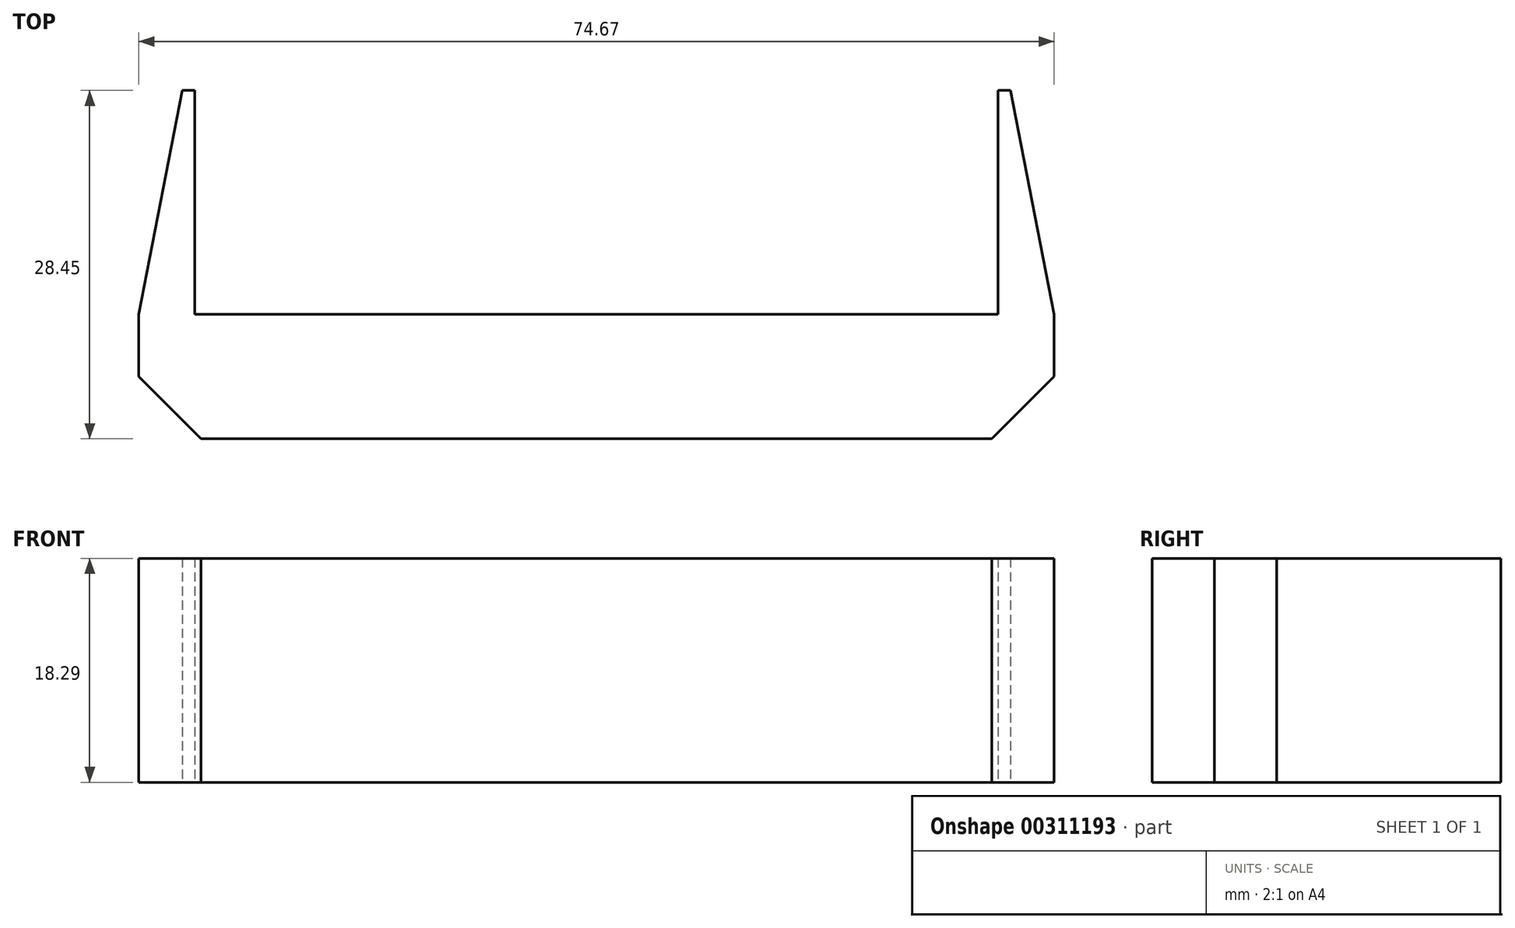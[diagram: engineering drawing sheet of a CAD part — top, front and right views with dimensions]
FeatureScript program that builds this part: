
annotation { "Feature Type Name" : "Feature", "Feature Type Description" : "" }
export const myFeature = defineFeature(function(context is Context, id is Id, definition is map)
    precondition{}
    {
        {
            var Q0;
            Q0=qCreatedBy(makeId("Top.planeOp"),FACE);
            var sketch = newSketch(context, id + "F0", { "sketchPlane" : qUnion([Q0])});
            skLineSegment(sketch, "E0.top", {"start": v(0, -18.29) * mm, "end": v(65.53, -18.29) * mm});
            skLineSegment(sketch, "E0.left", {"start": v(0, 0) * mm, "end": v(0, -18.29) * mm});
            skLineSegment(sketch, "E0.right", {"start": v(65.53, 0) * mm, "end": v(65.53, -18.29) * mm});
            skLineSegment(sketch, "E1", {"start": v(0, 0) * mm, "end": v(-1.02, 0) * mm});
            skLineSegment(sketch, "E2", {"start": v(66.55, 0) * mm, "end": v(65.53, 0) * mm});
            skLineSegment(sketch, "E3.top", {"start": v(-4.57, -28.45) * mm, "end": v(70.1, -28.45) * mm});
            skLineSegment(sketch, "E3.left", {"start": v(-4.57, -18.29) * mm, "end": v(-4.57, -28.45) * mm});
            skLineSegment(sketch, "E3.right", {"start": v(70.1, -18.29) * mm, "end": v(70.1, -28.45) * mm});
            skLineSegment(sketch, "E4", {"start": v(70.1, -18.29) * mm, "end": v(66.55, 0) * mm});
            skLineSegment(sketch, "E5", {"start": v(-4.57, -18.29) * mm, "end": v(-1.02, 0) * mm});
            skPoint(sketch, "E6.orphan", {"position": v(-2.03, 0) * mm});
            skPoint(sketch, "E7.0.end.orphan", {"position": v(-2.03, -18.29) * mm});
            skPoint(sketch, "E8.orphan", {"position": v(67.56, 0) * mm});
            skLineSegment(sketch, "E9.bottom", {"start": v(13.72, -28.45) * mm, "end": v(51.82, -28.45) * mm});
            skLineSegment(sketch, "E9.top", {"start": v(13.72, -79.25) * mm, "end": v(51.82, -79.25) * mm});
            skLineSegment(sketch, "E9.left", {"start": v(13.72, -28.45) * mm, "end": v(13.72, -79.25) * mm});
            skLineSegment(sketch, "E9.right", {"start": v(51.82, -28.45) * mm, "end": v(51.82, -79.25) * mm});
            skSolve(sketch);
        }
        {
            var Q0;
            Q0=makeQuery(id+"F0.imprint","IMPRINT",FACE,{"disambiguationData":[TD([[makeQuery(id+"F0.imprint","IMPRINT",EDGE,{"derivedFrom":sQuery(id+"F0.wireOp",EDGE,"E9.bottom")}),-1.0]])]});
            var Q1;
            Q1=makeQuery(id+"F0.imprint","IMPRINT",FACE,{"disambiguationData":[TD([[makeQuery(id+"F0.imprint","IMPRINT",EDGE,{"derivedFrom":sQuery(id+"F0.wireOp",EDGE,"E0.left")}),-1.0]])]});
            extrude(context, id + "F1", {"entities" : qUnion([Q0, Q1]), "depth" : 18.29 * mm});
        }
        {
            var Q0;
            Q0=makeQuery(id+"F1.opExtrude","CAP_EDGE",EDGE,{"disambiguationData":[OSD([sQuery(id+"F0.wireOp",EDGE,"E9.left")])],"isStart":false});
            var Q1;
            Q1=makeQuery(id+"F1.opExtrude","CAP_EDGE",EDGE,{"disambiguationData":[OSD([sQuery(id+"F0.wireOp",EDGE,"E9.right")])],"isStart":false});
            var Q2;
            Q2=makeQuery(id+"F1.opExtrude","CAP_EDGE",EDGE,{"disambiguationData":[OSD([sQuery(id+"F0.wireOp",EDGE,"E9.right")])],"isStart":true});
            var Q3;
            Q3=makeQuery(id+"F1.opExtrude","CAP_EDGE",EDGE,{"disambiguationData":[OSD([sQuery(id+"F0.wireOp",EDGE,"E9.left")])],"isStart":true});
            var Q4;
            Q4=makeQuery(id+"F1.opExtrude","SWEPT_EDGE",EDGE,{"disambiguationData":[OSD([sQuery(id+"F0.wireOp",EDGE,"E3.top"),sQuery(id+"F0.wireOp",EDGE,"E3.left")])]});
            var Q5;
            Q5=makeQuery(id+"F1.opExtrude","SWEPT_EDGE",EDGE,{"disambiguationData":[OSD([sQuery(id+"F0.wireOp",EDGE,"E3.top"),sQuery(id+"F0.wireOp",EDGE,"E3.right")])]});
            chamfer(context, id + "F2", {"entities" : qUnion([Q0, Q1, Q2, Q3, Q4, Q5]), "width" : 5.08 * mm, "tangentPropagation" : true});
        }
    });
